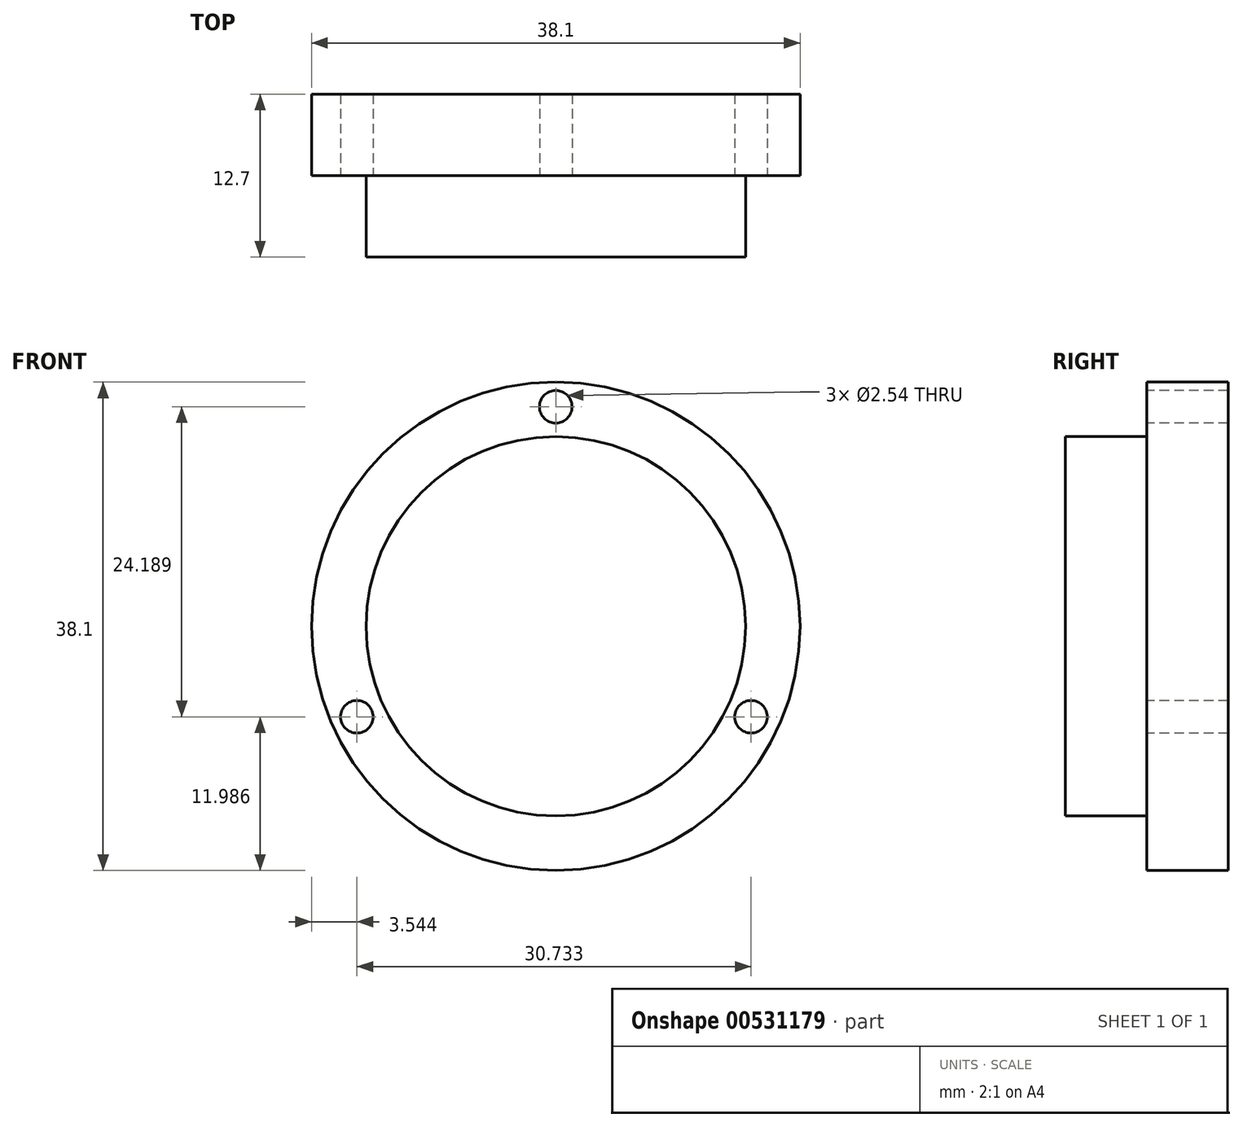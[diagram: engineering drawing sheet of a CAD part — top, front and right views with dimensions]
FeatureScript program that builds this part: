
annotation { "Feature Type Name" : "Feature", "Feature Type Description" : "" }
export const myFeature = defineFeature(function(context is Context, id is Id, definition is map)
    precondition{}
    {
        {
            var Q0;
            Q0=qCreatedBy(makeId("Front.planeOp"),FACE);
            var sketch = newSketch(context, id + "F0", { "sketchPlane" : qUnion([Q0])});
            skCircle(sketch, "E0", {"center": v(0, 0) * mm, "radius": 19.05 * mm});
            skSolve(sketch);
        }
        {
            var Q0;
            Q0=makeQuery(id+"F0.imprint","IMPRINT",FACE,{"disambiguationData":[TD([[makeQuery(id+"F0.imprint","IMPRINT",EDGE,{"derivedFrom":sQuery(id+"F0.wireOp",EDGE,"E0")}),1.0]])]});
            extrude(context, id + "F1", {"entities" : qUnion([Q0]), "depth" : 6.35 * mm, "offsetDistance" : 25.4 * mm});
        }
        {
            var Q0;
            Q0=qCreatedBy(makeId("Front.planeOp"),FACE);
            cPlane(context, id + "F2", {"entities" : qUnion([Q0]), "cplaneType" : CPlaneType.OFFSET, "offset" : 6.35 * mm, "width" : 152.4 * mm, "height" : 152.4 * mm});
        }
        {
            var Q0;
            Q0=qCreatedBy(id+"F2.planeOp",FACE);
            var sketch = newSketch(context, id + "F3", { "sketchPlane" : qUnion([Q0])});
            skCircle(sketch, "E1", {"center": v(0, 0) * mm, "radius": 14.8 * mm});
            skSolve(sketch);
        }
        {
            var Q0;
            Q0=makeQuery(id+"F3.imprint","IMPRINT",FACE,{"disambiguationData":[TD([[makeQuery(id+"F3.imprint","IMPRINT",EDGE,{"derivedFrom":sQuery(id+"F3.wireOp",EDGE,"E1")}),1.0]])]});
            extrude(context, id + "F4", {"entities" : qUnion([Q0]), "operationType" : NewBodyOperationType.ADD, "depth" : 6.35 * mm, "offsetDistance" : 25.4 * mm});
        }
        {
            var Q0;
            Q0=qCreatedBy(id+"F2.planeOp",FACE);
            var sketch = newSketch(context, id + "F5", { "sketchPlane" : qUnion([Q0])});
            skPoint(sketch, "E2", {"position": v(0, 17.12) * mm});
            skPoint(sketch, "E3", {"position": v(15.23, -7.06) * mm});
            skPoint(sketch, "E4", {"position": v(-15.5, -7.06) * mm});
            skSolve(sketch);
        }
        {
            var Q0;
            Q0=sQuery(id+"F5.wireOp",VERTEX,"E2");
            var Q1;
            Q1=sQuery(id+"F5.wireOp",VERTEX,"E3");
            var Q2;
            Q2=sQuery(id+"F5.wireOp",VERTEX,"E4");
            var Q3;
            Q3=makeQuery(id+"F1.opExtrude","SWEPT_BODY",BODY,{"disambiguationData":[OSD([sQuery(id+"F0.wireOp",EDGE,"E0")])]});
            hole(context, id + "F6", {"style" : HoleStyle.SIMPLE, "endStyle" : HoleEndStyle.THROUGH, "holeDiameter" : 2.54 * mm, "isTappedThrough" : true, "tappedDepth" : 12.7 * mm, "tapClearance" : 3, "locations" : qUnion([Q0, Q1, Q2]), "scope" : qUnion([Q3])});
        }
    });
